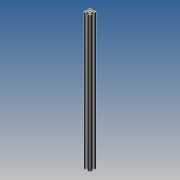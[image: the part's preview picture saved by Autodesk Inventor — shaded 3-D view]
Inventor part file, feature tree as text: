
AUTODESK INVENTOR PART (.ipt)
format: ipt  version: 2019 (Build 230136000, 136)  size: 237,568 bytes
history: native  units: mm
features: extrude x1, sketch x1, projected_geometry x1, other x1
ambient origin geometry x8: Origin, YZ Plane, XZ Plane, XY Plane, X Axis, Y Axis, Z Axis, Center Point
bodies: Solid1 (feature_tree)
feature tree (4):
  extrude  "Extrusion1"  [1 undecoded]
  sketch  "Sketch1"  dims[d0=300.0mm d1=0.0mm]
  projected_geometry  "Projected Loop1"
  parser-record x1  (decoder bookkeeping rows leaked as tree rows — omitted from the tree; the rows remain in map.json)
note: 1 required parameter value undecoded (feature->parameter linkage not recoverable at this tier; creation-order binding heuristic only, values carry confidence <= 0.55)
